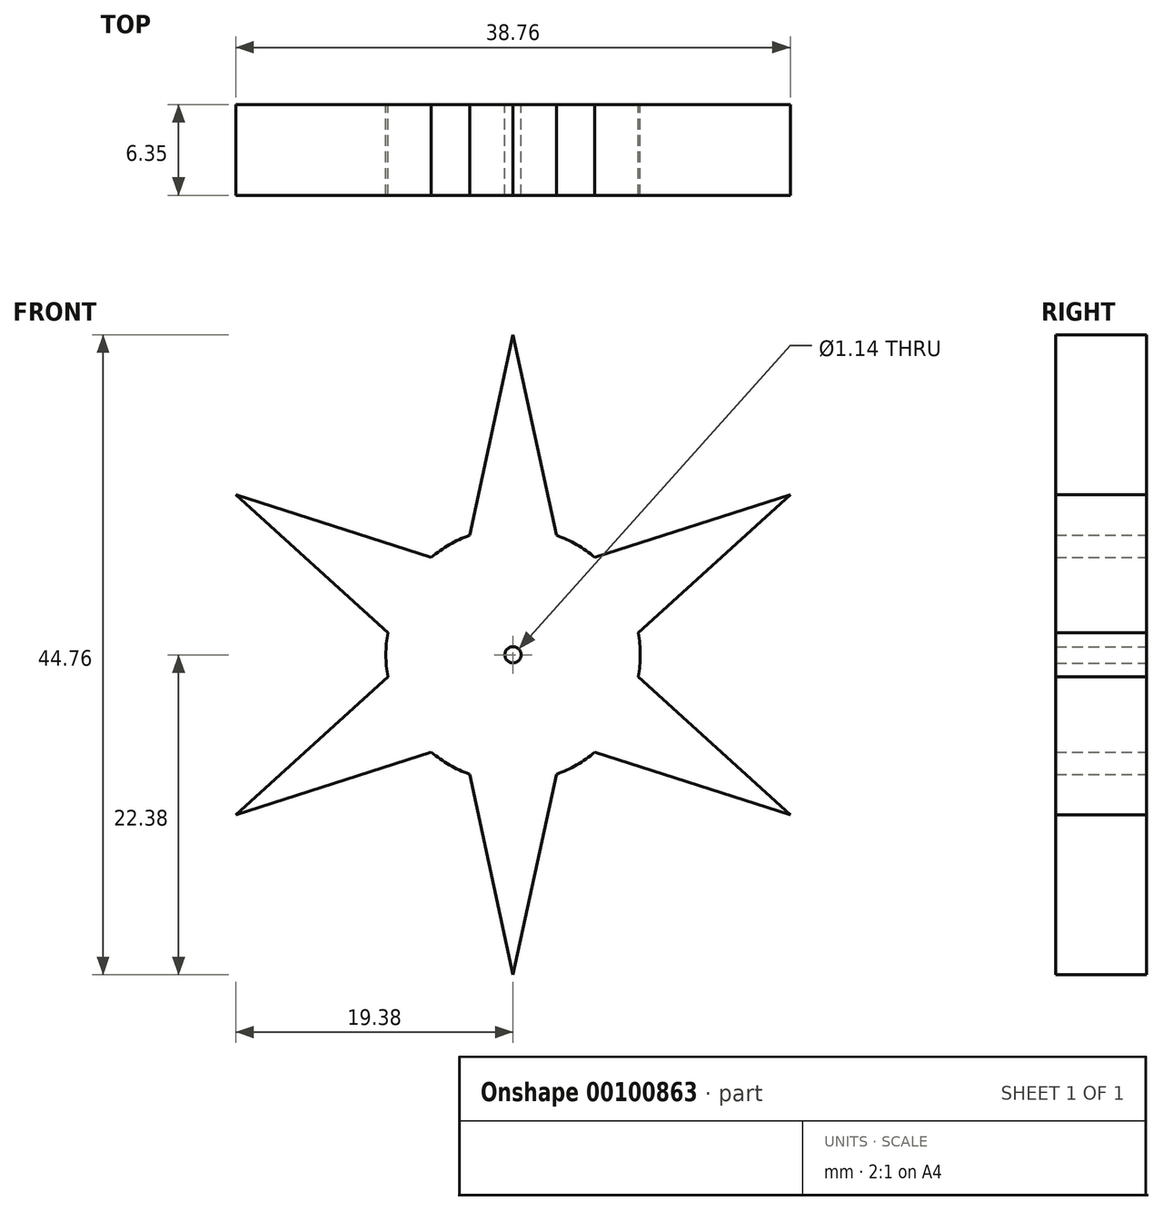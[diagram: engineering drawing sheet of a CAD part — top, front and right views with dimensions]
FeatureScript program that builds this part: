
annotation { "Feature Type Name" : "Feature", "Feature Type Description" : "" }
export const myFeature = defineFeature(function(context is Context, id is Id, definition is map)
    precondition{}
    {
        {
            var Q0;
            Q0=qCreatedBy(makeId("Front.planeOp"),FACE);
            var sketch = newSketch(context, id + "F0", { "sketchPlane" : qUnion([Q0])});
            skArc(sketch, "E0", {"start": v(-3.04, 8.35) * mm, "mid": v(-4.44, 7.7) * mm, "end": v(-5.71, 6.81) * mm});
            skCircle(sketch, "E1", {"center": v(0, 0) * mm, "radius": 0.57 * mm});
            skLineSegment(sketch, "E2", {"start": v(-3.04, 8.35) * mm, "end": v(0, 22.38) * mm});
            skLineSegment(sketch, "E3", {"start": v(0, 22.38) * mm, "end": v(3.04, 8.35) * mm});
            skArc(sketch, "E4", {"start": v(-3.04, 8.35) * mm, "mid": v(0, 8.9) * mm, "end": v(3.04, 8.35) * mm, "construction": true});
            skLineSegment(sketch, "E5", {"start": v(0, 0) * mm, "end": v(-3.04, 8.35) * mm, "construction": true});
            skLineSegment(sketch, "E6", {"start": v(0, 0) * mm, "end": v(3.04, 8.35) * mm, "construction": true});
            skLineSegment(sketch, "E7", {"start": v(0, 0) * mm, "end": v(8.9, 0) * mm, "construction": true});
            skLineSegment(sketch, "E8", {"start": v(8.9, 0) * mm, "end": v(23.24, 0) * mm, "construction": true});
            skLineSegment(sketch, "E9.1.0", {"start": v(-19.38, 11.19) * mm, "end": v(-5.71, 6.81) * mm});
            skLineSegment(sketch, "E9.1.1", {"start": v(-8.75, 1.54) * mm, "end": v(-19.38, 11.19) * mm});
            skLineSegment(sketch, "E9.2.0", {"start": v(-19.38, -11.19) * mm, "end": v(-8.75, -1.54) * mm});
            skLineSegment(sketch, "E9.2.1", {"start": v(-5.71, -6.81) * mm, "end": v(-19.38, -11.19) * mm});
            skLineSegment(sketch, "E9.3.0", {"start": v(0, -22.38) * mm, "end": v(-3.04, -8.35) * mm});
            skLineSegment(sketch, "E9.3.1", {"start": v(3.04, -8.35) * mm, "end": v(0, -22.38) * mm});
            skLineSegment(sketch, "E9.4.0", {"start": v(19.38, -11.19) * mm, "end": v(5.71, -6.81) * mm});
            skLineSegment(sketch, "E9.4.1", {"start": v(8.75, -1.54) * mm, "end": v(19.38, -11.19) * mm});
            skLineSegment(sketch, "E9.5.0", {"start": v(19.38, 11.19) * mm, "end": v(8.75, 1.54) * mm});
            skLineSegment(sketch, "E9.5.1", {"start": v(5.71, 6.81) * mm, "end": v(19.38, 11.19) * mm});
            skArc(sketch, "E10.trimOffspring", {"start": v(-8.75, 1.54) * mm, "mid": v(-8.9, 0) * mm, "end": v(-8.75, -1.54) * mm});
            skArc(sketch, "E11.trimOffspring", {"start": v(-5.71, -6.81) * mm, "mid": v(-4.45, -7.7) * mm, "end": v(-3.04, -8.35) * mm});
            skArc(sketch, "E12.trimOffspring", {"start": v(3.04, -8.35) * mm, "mid": v(4.44, -7.7) * mm, "end": v(5.71, -6.81) * mm});
            skArc(sketch, "E13.trimOffspring", {"start": v(8.75, -1.54) * mm, "mid": v(8.9, 0) * mm, "end": v(8.75, 1.54) * mm});
            skArc(sketch, "E14.trimOffspring", {"start": v(5.71, 6.81) * mm, "mid": v(4.45, 7.7) * mm, "end": v(3.04, 8.35) * mm});
            skSolve(sketch);
        }
        {
            var Q0;
            Q0=makeQuery(id+"F0.imprint","IMPRINT",FACE,{"disambiguationData":[TD([[makeQuery(id+"F0.imprint","IMPRINT",EDGE,{"derivedFrom":sQuery(id+"F0.wireOp",EDGE,"E0")}),1.0]])]});
            extrude(context, id + "F1", {"entities" : qUnion([Q0]), "depth" : 6.35 * mm});
        }
    });
